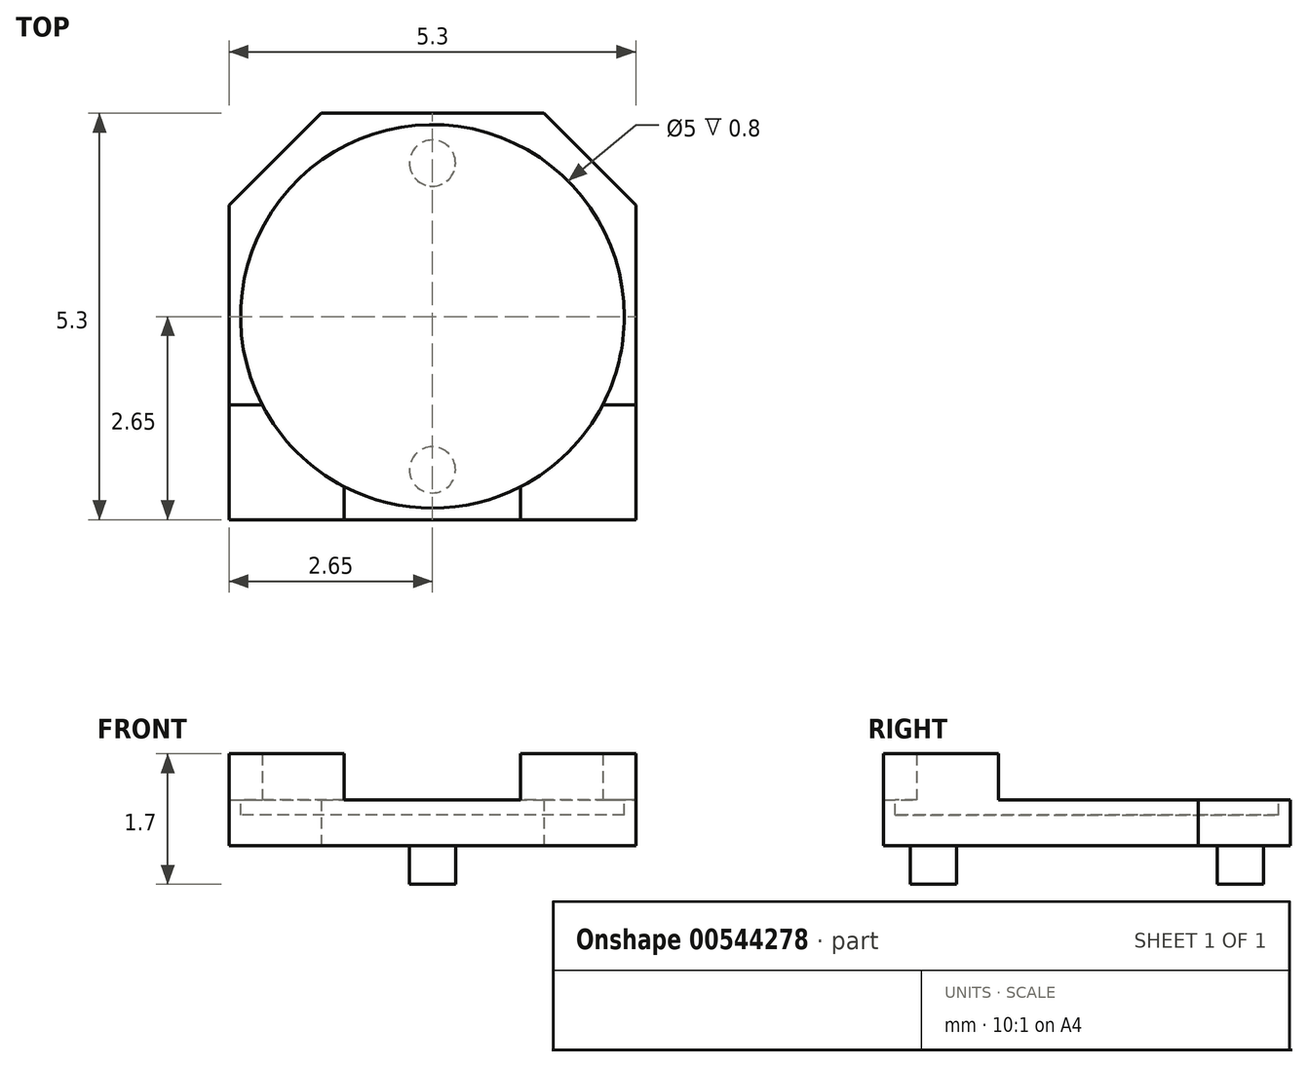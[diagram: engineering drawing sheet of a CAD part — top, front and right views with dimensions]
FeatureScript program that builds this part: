
annotation { "Feature Type Name" : "Feature", "Feature Type Description" : "" }
export const myFeature = defineFeature(function(context is Context, id is Id, definition is map)
    precondition{}
    {
        {
            var Q0;
            Q0=qCreatedBy(makeId("Top.planeOp"),FACE);
            var sketch = newSketch(context, id + "F0", { "sketchPlane" : qUnion([Q0])});
            skCircle(sketch, "E0", {"center": v(0, 0) * mm, "radius": 2.5 * mm, "construction": true});
            skLineSegment(sketch, "E1.bottom", {"start": v(-2.65, -2.65) * mm, "end": v(2.65, -2.65) * mm});
            skLineSegment(sketch, "E1.top", {"start": v(-1.45, 2.65) * mm, "end": v(1.45, 2.65) * mm});
            skLineSegment(sketch, "E1.left", {"start": v(-2.65, -2.65) * mm, "end": v(-2.65, 1.45) * mm});
            skLineSegment(sketch, "E1.right", {"start": v(2.65, -2.65) * mm, "end": v(2.65, 1.45) * mm});
            skLineSegment(sketch, "E2", {"start": v(-2.65, 1.45) * mm, "end": v(-1.45, 2.65) * mm});
            skLineSegment(sketch, "E3", {"start": v(1.45, 2.65) * mm, "end": v(2.65, 1.45) * mm});
            skSolve(sketch);
        }
        {
            var Q0;
            Q0=qSketchRegion(id+"F0",true);
            extrude(context, id + "F1", {"entities" : qUnion([Q0]), "depth" : 0.6 * mm});
        }
        {
            var Q0;
            Q0=makeQuery(id+"F1.opExtrude","CAP_FACE",FACE,{"disambiguationData":[OSD([sQuery(id+"F0.wireOp",EDGE,"E1.bottom"),sQuery(id+"F0.wireOp",EDGE,"E1.top"),sQuery(id+"F0.wireOp",EDGE,"E1.left"),sQuery(id+"F0.wireOp",EDGE,"E1.right"),sQuery(id+"F0.wireOp",EDGE,"E2"),sQuery(id+"F0.wireOp",EDGE,"E3")])],"isStart":false});
            var sketch = newSketch(context, id + "F2", { "sketchPlane" : qUnion([Q0])});
            skCircle(sketch, "E4", {"center": v(0, 0) * mm, "radius": 2.5 * mm});
            skSolve(sketch);
        }
        {
            var Q0;
            Q0=qSketchRegion(id+"F2",true);
            extrude(context, id + "F3", {"entities" : qUnion([Q0]), "operationType" : NewBodyOperationType.REMOVE, "oppositeDirection" : true, "depth" : 0.2 * mm});
        }
        {
            var Q0;
            Q0=makeQuery(id+"F1.opExtrude","CAP_FACE",FACE,{"disambiguationData":[OSD([sQuery(id+"F0.wireOp",EDGE,"E1.bottom"),sQuery(id+"F0.wireOp",EDGE,"E1.top"),sQuery(id+"F0.wireOp",EDGE,"E1.left"),sQuery(id+"F0.wireOp",EDGE,"E1.right"),sQuery(id+"F0.wireOp",EDGE,"E2"),sQuery(id+"F0.wireOp",EDGE,"E3")])],"isStart":false});
            var sketch = newSketch(context, id + "F4", { "sketchPlane" : qUnion([Q0])});
            skLineSegment(sketch, "E5", {"start": v(-2.65, -1.15) * mm, "end": v(-2.65, -2.65) * mm});
            skLineSegment(sketch, "E6", {"start": v(-2.65, -2.65) * mm, "end": v(-1.15, -2.65) * mm});
            skLineSegment(sketch, "E7", {"start": v(-1.15, -2.65) * mm, "end": v(-1.15, -2.22) * mm});
            skLineSegment(sketch, "E8", {"start": v(-2.65, -1.15) * mm, "end": v(-2.22, -1.15) * mm});
            skArc(sketch, "E9", {"start": v(-2.22, -1.15) * mm, "mid": v(-1.77, -1.77) * mm, "end": v(-1.15, -2.22) * mm});
            skLineSegment(sketch, "E10", {"start": v(2.65, -1.15) * mm, "end": v(2.22, -1.15) * mm});
            skLineSegment(sketch, "E11", {"start": v(2.65, -1.15) * mm, "end": v(2.65, -2.65) * mm});
            skLineSegment(sketch, "E12", {"start": v(2.65, -2.65) * mm, "end": v(1.15, -2.65) * mm});
            skLineSegment(sketch, "E13", {"start": v(1.15, -2.65) * mm, "end": v(1.15, -2.22) * mm});
            skArc(sketch, "E14", {"start": v(1.15, -2.22) * mm, "mid": v(1.77, -1.77) * mm, "end": v(2.22, -1.15) * mm});
            skSolve(sketch);
        }
        {
            var Q0;
            Q0=qSketchRegion(id+"F4",true);
            extrude(context, id + "F5", {"entities" : qUnion([Q0]), "operationType" : NewBodyOperationType.ADD, "depth" : 0.6 * mm});
        }
        {
            var Q0;
            Q0=makeQuery(id+"F1.opExtrude","CAP_FACE",FACE,{"disambiguationData":[OSD([sQuery(id+"F0.wireOp",EDGE,"E1.bottom"),sQuery(id+"F0.wireOp",EDGE,"E1.top"),sQuery(id+"F0.wireOp",EDGE,"E1.left"),sQuery(id+"F0.wireOp",EDGE,"E1.right"),sQuery(id+"F0.wireOp",EDGE,"E2"),sQuery(id+"F0.wireOp",EDGE,"E3")])],"isStart":true});
            var sketch = newSketch(context, id + "F6", { "sketchPlane" : qUnion([Q0])});
            skCircle(sketch, "E15", {"center": v(0, 2) * mm, "radius": 0.3 * mm});
            skCircle(sketch, "E16", {"center": v(0, -2) * mm, "radius": 0.3 * mm});
            skSolve(sketch);
        }
        {
            var Q0;
            Q0=qSketchRegion(id+"F6",true);
            extrude(context, id + "F7", {"entities" : qUnion([Q0]), "operationType" : NewBodyOperationType.ADD, "depth" : 0.5 * mm});
        }
    });
